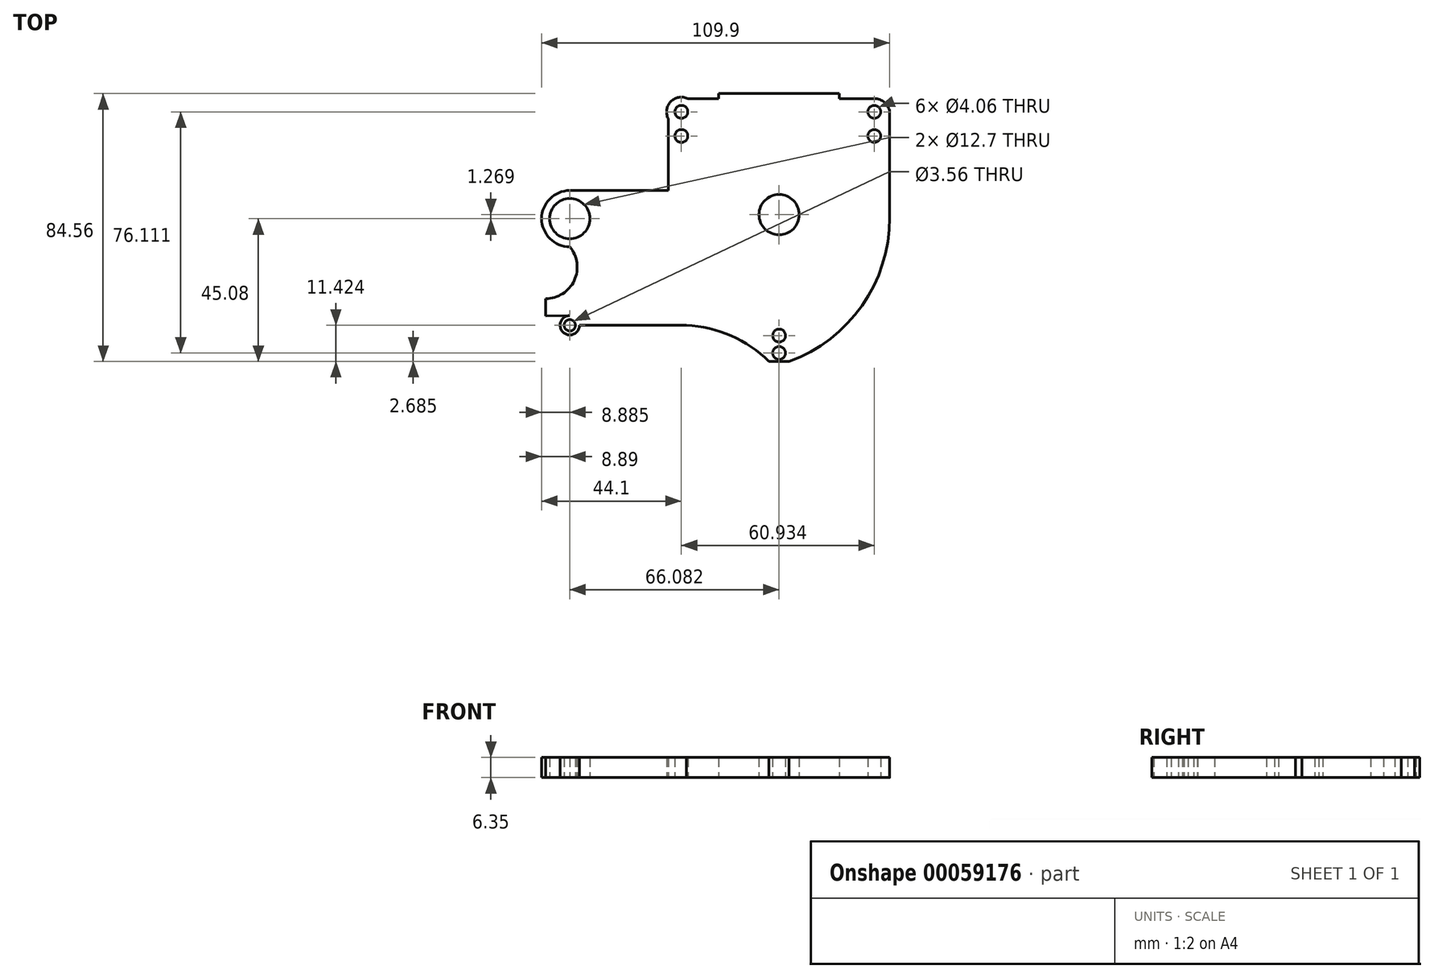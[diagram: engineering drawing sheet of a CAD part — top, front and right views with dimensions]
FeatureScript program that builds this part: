
annotation { "Feature Type Name" : "Feature", "Feature Type Description" : "" }
export const myFeature = defineFeature(function(context is Context, id is Id, definition is map)
    precondition{}
    {
        {
            var Q0;
            Q0=qCreatedBy(makeId("Top.planeOp"),FACE);
            var sketch = newSketch(context, id + "F0", { "sketchPlane" : qUnion([Q0])});
            skArc(sketch, "E0", {"start": v(16.41, -30.66) * mm, "mid": v(46.72, -5.82) * mm, "end": v(34.87, 31.54) * mm});
            skLineSegment(sketch, "E1", {"start": v(10.07, -30.8) * mm, "end": v(-49.8, -30.8) * mm});
            skLineSegment(sketch, "E2", {"start": v(13.24, -27.63) * mm, "end": v(12.56, -27.63) * mm});
            skLineSegment(sketch, "E3", {"start": v(-9.75, -22.4) * mm, "end": v(-52.84, -22.4) * mm});
            skCircle(sketch, "E4", {"center": v(-52.84, -30.8) * mm, "radius": 1.78 * mm});
            skArc(sketch, "E5", {"start": v(-52.9, -27.76) * mm, "mid": v(-54.98, -32.98) * mm, "end": v(-49.8, -30.8) * mm});
            skLineSegment(sketch, "E6", {"start": v(-5.8, 36.57) * mm, "end": v(-5.8, 42.33) * mm});
            skLineSegment(sketch, "E7", {"start": v(-5.8, 42.33) * mm, "end": v(32.3, 42.33) * mm});
            skLineSegment(sketch, "E8", {"start": v(32.3, 42.33) * mm, "end": v(32.3, 36.57) * mm});
            skArc(sketch, "E9", {"start": v(-8.39, 31.54) * mm, "mid": v(-21.78, 4.9) * mm, "end": v(-9.75, -22.4) * mm});
            skPoint(sketch, "E10.third.point", {"position": v(9.27, 35.62) * mm});
            skLineSegment(sketch, "E11", {"start": v(-52.84, -22.4) * mm, "end": v(-60.46, -22.4) * mm});
            skLineSegment(sketch, "E12", {"start": v(-60.46, -22.4) * mm, "end": v(-60.46, -27.83) * mm});
            skLineSegment(sketch, "E13", {"start": v(-60.46, -27.83) * mm, "end": v(-52.9, -27.76) * mm});
            skLineSegment(sketch, "E14", {"start": v(-8.39, 31.54) * mm, "end": v(-5.8, 36.57) * mm});
            skLineSegment(sketch, "E15", {"start": v(34.87, 31.54) * mm, "end": v(32.3, 36.57) * mm});
            skLineSegment(sketch, "E16", {"start": v(48.15, 3.13) * mm, "end": v(48.15, 5.11) * mm});
            skLineSegment(sketch, "E17.bottom", {"start": v(10.07, -30.8) * mm, "end": v(16.41, -30.8) * mm});
            skLineSegment(sketch, "E17.top", {"start": v(10.07, -42.23) * mm, "end": v(16.41, -42.23) * mm});
            skLineSegment(sketch, "E17.left", {"start": v(10.07, -30.8) * mm, "end": v(10.07, -42.23) * mm});
            skLineSegment(sketch, "E17.right", {"start": v(16.41, -30.8) * mm, "end": v(16.41, -42.23) * mm});
            skLineSegment(sketch, "E18", {"start": v(16.41, -30.66) * mm, "end": v(16.41, -30.8) * mm});
            skLineSegment(sketch, "E19", {"start": v(13.24, -42.23) * mm, "end": v(13.24, -30.8) * mm});
            skCircle(sketch, "E20", {"center": v(13.24, -34.06) * mm, "radius": 2.03 * mm});
            skCircle(sketch, "E21", {"center": v(13.24, -39.55) * mm, "radius": 2.03 * mm});
            skArc(sketch, "E22", {"start": v(16.41, -42.23) * mm, "mid": v(39.43, -24.55) * mm, "end": v(48.15, 3.13) * mm});
            skArc(sketch, "E23", {"start": v(10.07, -42.23) * mm, "mid": v(-3.7, -33.39) * mm, "end": v(-19.86, -30.8) * mm});
            skLineSegment(sketch, "E24", {"start": v(43.3, 36.57) * mm, "end": v(41.27, 36.57) * mm});
            skPoint(sketch, "E24.endSnap0", {"position": v(-17.63, 35.47) * mm});
            skCircle(sketch, "E25", {"center": v(-17.63, 36.57) * mm, "radius": 2.03 * mm});
            skCircle(sketch, "E26", {"center": v(43.3, 36.57) * mm, "radius": 2.03 * mm});
            skLineSegment(sketch, "E27", {"start": v(-17.63, 36.57) * mm, "end": v(-17.63, 28.95) * mm});
            skLineSegment(sketch, "E28", {"start": v(43.3, 36.57) * mm, "end": v(43.3, 28.95) * mm});
            skCircle(sketch, "E29", {"center": v(-17.63, 28.95) * mm, "radius": 2.03 * mm});
            skCircle(sketch, "E30", {"center": v(43.3, 28.95) * mm, "radius": 2.03 * mm});
            skPoint(sketch, "E31.start.orphan", {"position": v(-21.78, 4.9) * mm});
            skLineSegment(sketch, "E32", {"start": v(-21.78, 4.9) * mm, "end": v(-21.78, 36.57) * mm});
            skPoint(sketch, "E33.start.orphan", {"position": v(-20.83, 42.33) * mm});
            skPoint(sketch, "E34.orphan", {"position": v(48.15, 42.33) * mm});
            skPoint(sketch, "E35.start.orphan", {"position": v(-17.63, 42.33) * mm});
            skArc(sketch, "E36", {"start": v(-15.58, 40.74) * mm, "mid": v(-20.94, 39.83) * mm, "end": v(-21.78, 34.46) * mm});
            skLineSegment(sketch, "E37", {"start": v(-19.68, 40.74) * mm, "end": v(-5.8, 40.74) * mm});
            skLineSegment(sketch, "E38", {"start": v(48.15, 5.11) * mm, "end": v(48.15, 36.57) * mm});
            skPoint(sketch, "E39.end.orphan", {"position": v(43.3, 41.42) * mm});
            skLineSegment(sketch, "E40", {"start": v(-5.8, 40.74) * mm, "end": v(43.3, 40.74) * mm});
            skArc(sketch, "E41", {"start": v(48.15, 36.57) * mm, "mid": v(46.5, 39.55) * mm, "end": v(43.3, 40.74) * mm});
            skLineSegment(sketch, "E42.trimOffspring", {"start": v(-15.6, 36.57) * mm, "end": v(-17.63, 36.57) * mm});
            skCircle(sketch, "E43", {"center": v(-52.84, 2.85) * mm, "radius": 6.35 * mm});
            skArc(sketch, "E44", {"start": v(-52.84, 11.74) * mm, "mid": v(-61.73, 2.85) * mm, "end": v(-52.84, -6.04) * mm});
            skLineSegment(sketch, "E45", {"start": v(-52.84, 11.74) * mm, "end": v(-21.78, 11.74) * mm});
            skLineSegment(sketch, "E46", {"start": v(-52.84, -6.04) * mm, "end": v(-20.31, -6.04) * mm});
            skCircle(sketch, "E47", {"center": v(13.24, 4.12) * mm, "radius": 6.35 * mm});
            skArc(sketch, "E48", {"start": v(-60.46, -22.4) * mm, "mid": v(-51.44, -16.65) * mm, "end": v(-52.84, -6.04) * mm});
            skSolve(sketch);
        }
        {
            var Q0;
            Q0 = qSketchRegion(id + "F0", true);
            extrude(context, id + "F1", {"entities" : qUnion([Q0]), "depth" : 6.35 * mm});
        }
    });
